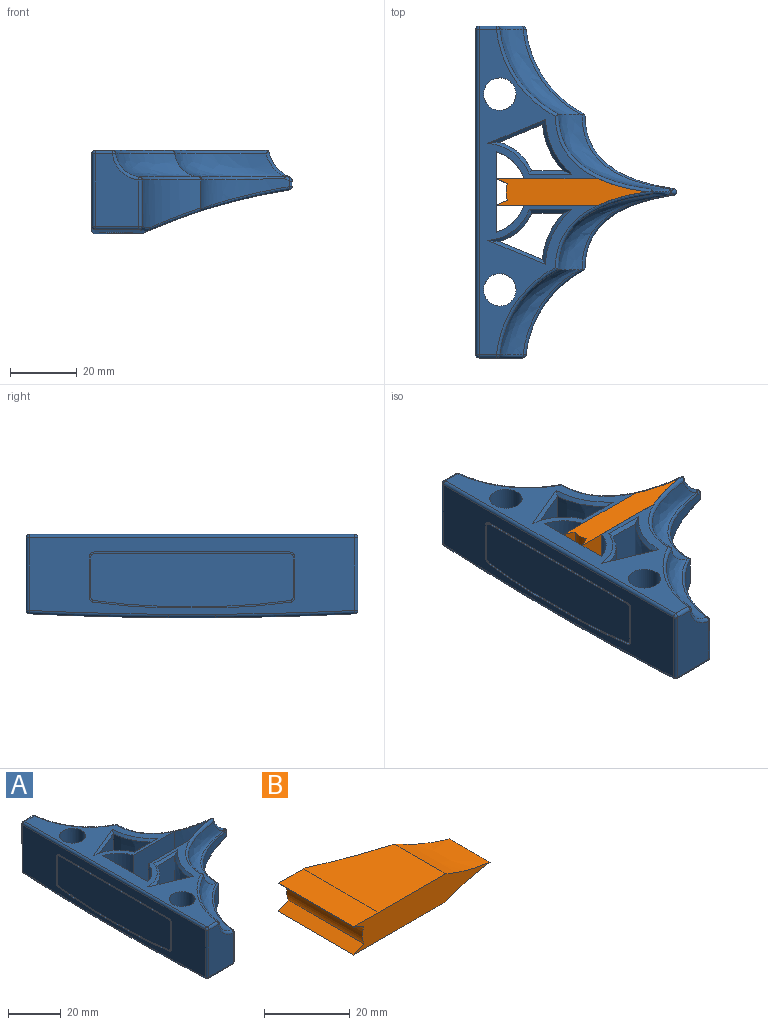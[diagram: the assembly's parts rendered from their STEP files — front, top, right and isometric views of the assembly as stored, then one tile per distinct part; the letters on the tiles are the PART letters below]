
ASSEMBLY  parts=2 mates=1
PART A: 153 faces, bbox 75.6x106.4x26.5 mm
  f0: cylinder r=1017.26mm len=41.73mm, axis (-1,0,0), area 463mm2, adj f4,f9,f10,f18,f19,f59,f62,f66
  f1: extruded ~78.9x44.16mm, area 688.8mm2, adj f4,f5,f6,f14,f15,f30,f31,f55
  f2: plane 98.22x36.48mm, normal (0,0,1), area 999.6mm2, adj f18,f19,f20,f28,f45,f46,f47,f48
  f3: cylinder r=1017.26mm len=41.73mm, axis (-1,0,0), area 463mm2, adj f5,f6,f10,f11,f19,f20,f74,f77
  f4: bspline ~24.86x0.64mm, area 1.5mm2, adj f0,f1,f9,f55,f128
  f5: bspline ~38.34x2.44mm, area 8.5mm2, adj f1,f3,f80,f137
  f6: bspline ~24.86x0.64mm, area 1.5mm2, adj f1,f3,f11,f56,f142
  f7: plane 21.86x13.09mm, normal (0,-1,0), area 239.9mm2, adj f16,f44,f71,f75,f77
  f8: plane 21.86x13.09mm, normal (0,1,0), area 239.9mm2, adj f17,f49,f63,f66,f67
  f9: plane 3.25x2.15mm, normal (0,0,-1), area 3.5mm2, adj f0,f4,f18,f55
  f10: plane 14.28x5.19mm, normal (0,0,-1), area 74.1mm2, adj f0,f3,f19,f72
  f11: plane 3.25x2.15mm, normal (0,0,-1), area 3.5mm2, adj f3,f6,f20,f56
  f12: cylinder r=32.41mm len=25.62mm, axis (0,0,-1), area 403.4mm2, adj f14,f17,f22,f51,f52,f62
  f13: cylinder r=32.41mm len=25.62mm, axis (0,0,-1), area 403.4mm2, adj f15,f16,f21,f41,f42,f79
  f14: bspline ~20.31x18.84mm, area 31mm2, adj f1,f12,f22,f30,f61
  f15: bspline ~20.31x18.84mm, area 31mm2, adj f1,f13,f21,f31,f80
  f16: cylinder r=1mm len=13.96mm, axis (0,0,-1), area 20.5mm2, adj f7,f13,f43,f78
  f17: cylinder r=1mm len=13.96mm, axis (0,0,-1), area 20.5mm2, adj f8,f12,f50,f64
  f18: cylinder r=12.62mm len=25mm, axis (0,0,1), area 299.6mm2, adj f0,f2,f9,f19,f55
  f19: plane 25x24.12mm, normal (1,0,0), area 602.9mm2, adj f0,f2,f3,f10,f18,f20
  f20: cylinder r=12.62mm len=25mm, axis (0,0,1), area 299.6mm2, adj f2,f3,f11,f19,f56
  f21: extruded ~26.53x22.32mm, area 226.3mm2, adj f13,f15,f29,f31,f34,f41
  f22: extruded ~26.53x22.32mm, area 226.3mm2, adj f12,f14,f29,f30,f37,f52
  f23: plane 97.65x23mm, normal (-1,0,0), area 1206.4mm2, adj f28,f67,f70,f72,f74,f75,f81,f82
  f24: bspline ~26.51x25.72mm, area 306.2mm2, adj f25,f48,f49,f51
  f25: bspline ~50.36x23.31mm, area 337.7mm2, adj f24,f38,f47,f48,f51,f52,f53
  f26: bspline ~50.36x23.31mm, area 337.7mm2, adj f27,f36,f40,f41,f42,f45,f46
  f27: bspline ~26.51x25.72mm, area 306.2mm2, adj f26,f42,f44,f45
  f28: cylinder r=1mm len=97.65mm, axis (0,1,0), area 153.4mm2, adj f2,f23,f65,f73
  f29: cylinder r=1mm len=1.98mm, axis (0,0,-1), area 4.8mm2, adj f21,f22,f32,f35
  f30: bspline ~31.83x24.12mm, area 55.3mm2, adj f1,f14,f22,f32
  f31: bspline ~31.83x24.12mm, area 55.3mm2, adj f1,f15,f21,f32
  f32: sphere r=1mm, area 1.7mm2, adj f29,f30,f31
  f33: cylinder r=11.85mm len=0.01mm, axis (0,1,0), area 0mm2, adj f34,f36,f37,f38
  f34: bspline ~2.98x2.36mm, area 1.7mm2, adj f21,f33,f35,f39,f40
  f35: bspline ~7.81x2.68mm, area 3.1mm2, adj f29,f34,f37
  f36: bspline ~8.56x6.92mm, area 12.4mm2, adj f26,f33,f38,f39,f46
  f37: bspline ~2.98x2.36mm, area 1.7mm2, adj f22,f33,f35,f53,f54
  f38: bspline ~8.66x7.03mm, area 12.4mm2, adj f25,f33,f36,f47,f54
  f39: bspline ~1.13x0.72mm, area 0.1mm2, adj f34,f36,f40
  f40: bspline ~0.8x0.57mm, area 0.2mm2, adj f26,f34,f39,f41
  f41: bspline ~31.81x23.16mm, area 44.8mm2, adj f13,f21,f26,f40,f42
  f42: bspline ~28.37x19.43mm, area 44.7mm2, adj f13,f26,f27,f41,f43
  f43: sphere r=1mm, area 1.4mm2, adj f16,f42,f44
  f44: bspline ~8.62x8.2mm, area 16.9mm2, adj f7,f27,f43,f68
  f45: bspline ~27.48x19.33mm, area 48.3mm2, adj f2,f26,f27,f46,f68
  f46: bspline ~32.48x25.47mm, area 60.1mm2, adj f2,f26,f36,f45,f47,f57
  f47: bspline ~32.48x25.47mm, area 60.1mm2, adj f2,f25,f38,f46,f48,f58
  f48: bspline ~27.48x19.33mm, area 48.3mm2, adj f2,f24,f25,f47,f60
  f49: bspline ~8.62x8.2mm, area 16.9mm2, adj f8,f24,f50,f60
  f50: sphere r=1mm, area 1.4mm2, adj f17,f49,f51
  f51: bspline ~28.37x19.43mm, area 44.7mm2, adj f12,f24,f25,f50,f52
  f52: bspline ~31.81x23.16mm, area 44.8mm2, adj f12,f22,f25,f51,f53
  f53: bspline ~0.8x0.57mm, area 0.2mm2, adj f25,f37,f52,f54
  f54: bspline ~1.13x0.72mm, area 0.1mm2, adj f37,f38,f53
  f55: plane 25.08x22.32mm, normal (0,-1,0), area 462.9mm2, adj f1,f2,f4,f9,f18,f58
  f56: plane 25x22.38mm, normal (0,1,0), area 462.9mm2, adj f1,f2,f6,f11,f20,f57
  f57: extruded ~16.99x14.58mm, area 230.1mm2, adj f1,f46,f56,f58
  f58: extruded ~16.99x14.58mm, area 230.1mm2, adj f1,f47,f55,f57
  f59: bspline ~48.61x3.57mm, area 8.5mm2, adj f0,f1,f61,f134
  f60: sphere r=1mm, area 0.8mm2, adj f48,f49,f63
  f61: sphere r=1mm, area 0.2mm2, adj f14,f59,f62
  f62: bspline ~14.03x3.85mm, area 14.9mm2, adj f0,f12,f61,f64
  f63: cylinder r=1mm len=5.19mm, axis (1,0,0), area 8.2mm2, adj f2,f8,f60,f65
  f64: sphere r=1mm, area 1.4mm2, adj f17,f62,f66
  f65: sphere r=1mm, area 1.6mm2, adj f28,f63,f67
  f66: cylinder r=1mm len=13.09mm, axis (-1,0,0), area 19.9mm2, adj f0,f8,f64,f69
  f67: cylinder r=1mm len=21.85mm, axis (0,0,1), area 34.3mm2, adj f8,f23,f65,f69
  f68: sphere r=1mm, area 1.4mm2, adj f44,f45,f71
  f69: sphere r=1mm, area 1mm2, adj f66,f67,f70
  f70: torus R=1016.26mm, axis (1,0,0), area 65.6mm2, adj f0,f23,f69,f72
  f71: cylinder r=1mm len=5.19mm, axis (-1,0,0), area 8.2mm2, adj f2,f7,f68,f73
  f72: cylinder r=1mm len=14.28mm, axis (0,-1,0), area 22.4mm2, adj f10,f23,f70,f74
  f73: sphere r=1mm, area 1.6mm2, adj f28,f71,f75
  f74: torus R=1016.26mm, axis (1,0,0), area 65.6mm2, adj f3,f23,f72,f76
  f75: cylinder r=1mm len=21.85mm, axis (0,0,-1), area 34.3mm2, adj f7,f23,f73,f76
  f76: sphere r=1mm, area 1mm2, adj f74,f75,f77
  f77: cylinder r=1mm len=13.09mm, axis (-1,0,0), area 19.9mm2, adj f3,f7,f76,f78
  f78: sphere r=1mm, area 1.4mm2, adj f16,f77,f79
  f79: bspline ~16.55x5.07mm, area 14.9mm2, adj f3,f13,f78,f80
  f80: sphere r=1mm, area 0.2mm2, adj f5,f15,f79
  f81: plane 12.08x0.5mm, normal (0,1,0), area 6mm2, adj f23,f82,f98,f99
  f82: cylinder r=1.5mm len=1.5mm, axis (-1,0,0), area 1.2mm2, adj f23,f81,f83,f99
  f83: plane 58.73x0.5mm, normal (0,0,-1), area 29.4mm2, adj f23,f82,f84,f99
  f84: cylinder r=1.5mm len=1.5mm, axis (-1,0,0), area 1.2mm2, adj f23,f83,f85,f99
  f85: plane 12.08x0.5mm, normal (0,-1,0), area 6mm2, adj f23,f84,f86,f99
  f86: cylinder r=1.5mm len=1.48mm, axis (-1,0,0), area 1.1mm2, adj f23,f85,f87,f99
  f87: cylinder r=175.4mm len=29.58mm, axis (-1,0,0), area 14.8mm2, adj f23,f86,f88,f99
  f88: cylinder r=175.4mm len=29.58mm, axis (-1,0,0), area 14.8mm2, adj f23,f87,f98,f99
  f89: cylinder r=1mm len=0.99mm, axis (-1,0,0), area 0.7mm2, adj f90,f97,f99,f100
  f90: cylinder r=174.9mm len=29.51mm, axis (-1,0,0), area 14.8mm2, adj f89,f91,f99,f100
  f91: cylinder r=174.9mm len=29.51mm, axis (-1,0,0), area 14.8mm2, adj f90,f92,f99,f100
  f92: cylinder r=1mm len=0.99mm, axis (-1,0,0), area 0.7mm2, adj f91,f93,f99,f100
  f93: plane 12.08x0.5mm, normal (0,1,0), area 6mm2, adj f92,f94,f99,f100
  f94: cylinder r=1mm len=1mm, axis (-1,0,0), area 0.8mm2, adj f93,f95,f99,f100
  f95: plane 58.73x0.5mm, normal (0,0,1), area 29.4mm2, adj f94,f96,f99,f100
  f96: cylinder r=1mm len=1mm, axis (-1,0,0), area 0.8mm2, adj f95,f97,f99,f100
  f97: plane 12.08x0.5mm, normal (0,-1,0), area 6mm2, adj f89,f96,f99,f100
  f98: cylinder r=1.5mm len=1.48mm, axis (-1,0,0), area 1.1mm2, adj f23,f81,f88,f99
  f99: plane 61.73x16.84mm, normal (-1,0,0), area 74.8mm2, adj f81,f82,f83,f84,f85,f86,f87,f88
  f100: plane 60.73x15.84mm, normal (-1,0,0), area 928.7mm2, adj f89,f90,f91,f92,f93,f94,f95,f96
  f101: plane 23.22x13.29mm, normal (0.38,0.92,0), area 319.6mm2, adj f102,f104,f123,f135,f136,f137,f139
  f102: extruded ~20.8x13.97mm, area 307.4mm2, adj f101,f103,f124,f136
  f103: plane 22.46x9.86mm, normal (0,-1,0), area 196.7mm2, adj f102,f104,f126,f136,f138
  f104: cylinder r=15.62mm len=23.28mm, axis (0,0,1), area 310.1mm2, adj f101,f103,f125,f138,f140,f141,f142
  f105: plane 22.46x9.86mm, normal (0,1,0), area 196.7mm2, adj f106,f108,f120,f129,f131
  f106: extruded ~20.8x13.97mm, area 307.4mm2, adj f105,f107,f122,f131
  f107: plane 23.21x13.29mm, normal (0.38,-0.92,0), area 319.5mm2, adj f106,f108,f121,f131,f132,f133,f134
  f108: cylinder r=15.62mm len=23.28mm, axis (0,0,1), area 309.9mm2, adj f105,f107,f119,f127,f128,f129,f130
  f109: extruded ~11.89x6.79mm, area 78.2mm2, adj f110,f112,f113,f144,f145,f146
  f110: plane 6.63x4.92mm, normal (0.39,0.92,0), area 28.9mm2, adj f109,f111,f113,f143,f145
  f111: extruded ~13.54x4.6mm, area 56.5mm2, adj f110,f112,f113,f143
  f112: plane 4.62x3.82mm, normal (0,-1,0), area 14.5mm2, adj f109,f111,f113,f143,f144
  f113: plane 13.54x8.87mm, normal (0,0,-1), area 55mm2, adj f109,f110,f111,f112
  f114: plane 6.63x4.92mm, normal (0.39,-0.92,0), area 28.9mm2, adj f115,f117,f118,f149,f150
  f115: extruded ~11.89x6.79mm, area 78.2mm2, adj f114,f116,f118,f147,f148,f150
  f116: plane 4.62x3.82mm, normal (0,1,0), area 14.5mm2, adj f115,f117,f118,f147,f149
  f117: extruded ~13.54x4.6mm, area 56.5mm2, adj f114,f116,f118,f149
  f118: plane 13.54x8.87mm, normal (0,0,-1), area 55mm2, adj f114,f115,f116,f117
  f119: cone r=14.62mm half-angle=45deg, axis (0,0,-1), area 21.1mm2, adj f2,f108,f120,f121
  f120: plane 12.66x1.02mm, normal (0,0.71,0.71), area 15.7mm2, adj f2,f105,f119,f122
  f121: plane 17.41x7.33mm, normal (0.27,-0.65,0.71), area 23mm2, adj f2,f107,f119,f122
  f122: bspline ~18.72x9.62mm, area 24.3mm2, adj f2,f106,f120,f121
  f123: plane 17.41x7.33mm, normal (0.27,0.65,0.71), area 23mm2, adj f2,f101,f124,f125
  f124: bspline ~18.72x9.62mm, area 24.3mm2, adj f2,f102,f123,f126
  f125: cone r=14.62mm half-angle=45deg, axis (0,0,-1), area 21.1mm2, adj f2,f104,f123,f126
  f126: plane 12.66x1.02mm, normal (0,-0.71,0.71), area 15.7mm2, adj f2,f103,f124,f125
  f127: bspline ~3x1.74mm, area 2.4mm2, adj f1,f108,f128,f129
  f128: bspline ~0.73x0.71mm, area 0.3mm2, adj f4,f108,f127,f130
  f129: bspline ~11.99x5.27mm, area 11.5mm2, adj f1,f105,f108,f127,f131
  f130: bspline ~11.25x7.13mm, area 11.4mm2, adj f0,f108,f128,f132
  f131: bspline ~17.74x9.08mm, area 19.3mm2, adj f1,f105,f106,f107,f129,f133
  f132: bspline ~10.65x4.98mm, area 10.2mm2, adj f0,f107,f130,f134
  f133: bspline ~5.36x2.93mm, area 5.5mm2, adj f1,f107,f131,f134
  f134: bspline ~0.74x0.71mm, area 0.3mm2, adj f59,f107,f132,f133
  f135: bspline ~5.36x2.93mm, area 5.5mm2, adj f1,f101,f136,f137
  f136: bspline ~17.74x9.08mm, area 19.3mm2, adj f1,f101,f102,f103,f135,f138
  f137: bspline ~0.74x0.71mm, area 0.3mm2, adj f5,f101,f135,f139
  f138: bspline ~11.99x5.27mm, area 11.5mm2, adj f1,f103,f104,f136,f140
  f139: bspline ~11.17x5.2mm, area 10.2mm2, adj f3,f101,f137,f141
  f140: bspline ~3x1.74mm, area 2.4mm2, adj f1,f104,f138,f142
  f141: bspline ~11.25x7.13mm, area 11.4mm2, adj f3,f104,f139,f142
  f142: bspline ~0.73x0.71mm, area 0.3mm2, adj f6,f104,f140,f141
  f143: bspline ~17.22x6.37mm, area 17.5mm2, adj f1,f110,f111,f112,f144,f145
  f144: bspline ~5.51x2.4mm, area 4.7mm2, adj f1,f109,f112,f143,f146
  f145: bspline ~6.08x3.25mm, area 5.8mm2, adj f1,f109,f110,f143,f146
  f146: bspline ~14.01x6.53mm, area 11.7mm2, adj f1,f109,f144,f145
  f147: bspline ~5.51x2.41mm, area 4.7mm2, adj f1,f115,f116,f148,f149
  f148: bspline ~12.79x5.96mm, area 11.7mm2, adj f1,f115,f147,f150
  f149: bspline ~17.22x6.37mm, area 17.5mm2, adj f1,f114,f116,f117,f147,f150
  f150: bspline ~6.08x3.25mm, area 5.8mm2, adj f1,f114,f115,f148,f149
  f151: cylinder r=4.87mm len=24.6mm, axis (0,0,1), area 753.5mm2, adj f0,f2
  f152: cylinder r=4.87mm len=24.6mm, axis (0,0,1), area 753.5mm2, adj f2,f3
PART B: 12 faces, bbox 45.4x25.3x8.4 mm
  f0: extruded ~16.99x14.58mm, area 230.1mm2, adj f6,f7,f9,f10
  f1: plane 25x22.23mm, normal (0,0,1), area 462.9mm2, adj f5,f6,f7,f8,f9
  f2: plane 25x3.43mm, normal (-0.41,0,-0.91), area 93.8mm2, adj f3,f7,f8,f11
  f3: cylinder r=6.02mm len=25mm, axis (0,1,0), area 126.9mm2, adj f2,f4,f7,f8
  f4: plane 25x3.43mm, normal (-0.41,0,0.91), area 93.8mm2, adj f3,f7,f8,f10
  f5: plane 25x8.27mm, normal (0.01,0,1), area 206.6mm2, adj f1,f7,f8,f11
  f6: extruded ~36.27x11.65mm, area 245.1mm2, adj f0,f1,f8,f9,f10
  f7: plane 45.41x8.43mm, normal (0,-1,0), area 270.9mm2, adj f0,f1,f2,f3,f4,f5,f9,f10
  f8: plane 8.81x8.1mm, normal (0,1,0), area 50.5mm2, adj f1,f2,f3,f4,f5,f6,f10,f11
  f9: extruded ~16.99x14.58mm, area 230.1mm2, adj f0,f1,f6,f7
  f10: plane 30.5x25mm, normal (0,0,-1), area 669.5mm2, adj f0,f4,f6,f7,f8
  f11: plane 25x0.1mm, normal (-1,0,0), area 2.4mm2, adj f2,f5,f7,f8
PLACE A at identity
PLACE B rot(axis=(-1,0,0),90deg) t=(0,0,0)mm
MATE fastened B.f7 <-> A.f2  axis (0,0,1) through (-85.04,-7.14,25)mm
